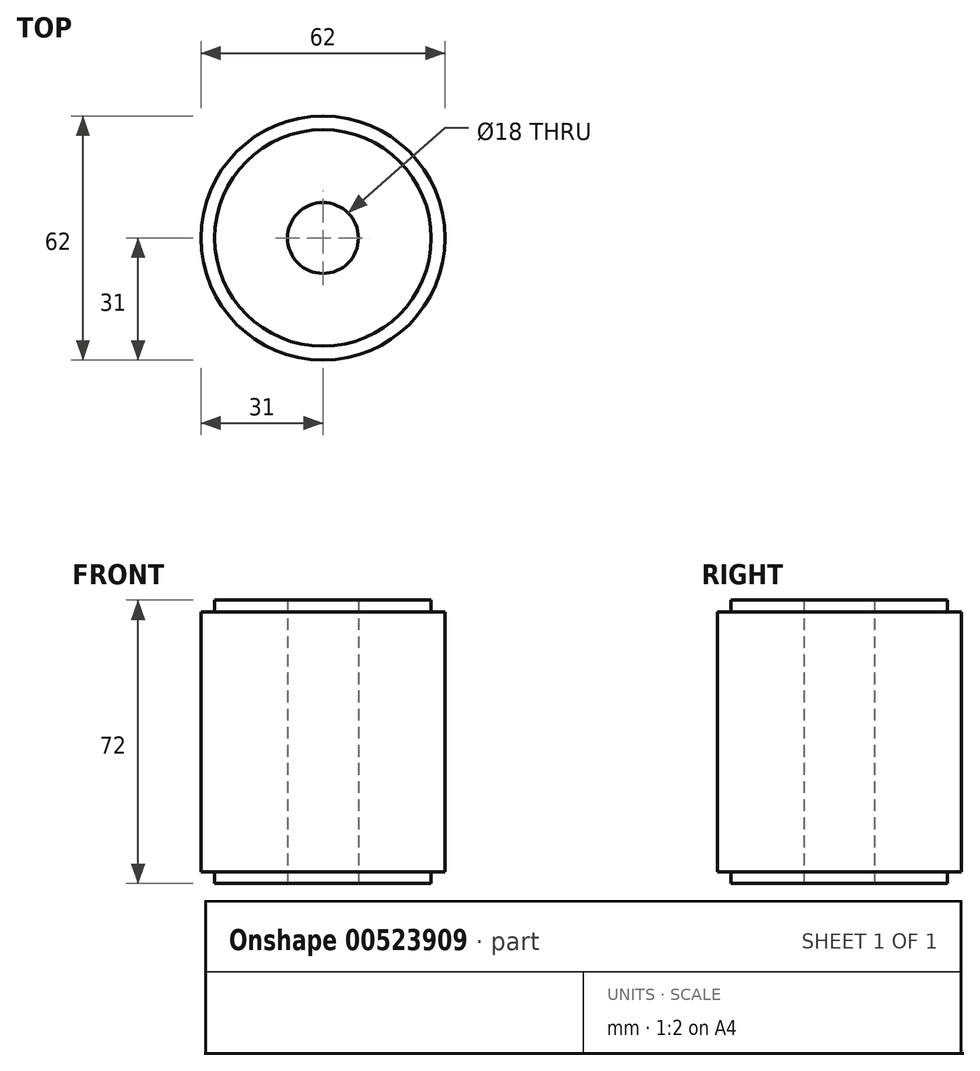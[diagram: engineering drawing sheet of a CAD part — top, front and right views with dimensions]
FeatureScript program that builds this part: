
annotation { "Feature Type Name" : "Feature", "Feature Type Description" : "" }
export const myFeature = defineFeature(function(context is Context, id is Id, definition is map)
    precondition{}
    {
        {
            var Q0;
            Q0=qCreatedBy(makeId("Top.planeOp"),FACE);
            var sketch = newSketch(context, id + "F0", { "sketchPlane" : qUnion([Q0])});
            skCircle(sketch, "E0", {"center": v(0, 0) * mm, "radius": 31 * mm});
            skCircle(sketch, "E1", {"center": v(0, 0) * mm, "radius": 27.5 * mm});
            skCircle(sketch, "E2", {"center": v(0, 0) * mm, "radius": 9 * mm});
            skSolve(sketch);
        }
        {
            var Q0;
            Q0=makeQuery(id+"F0.imprint","IMPRINT",FACE,{"disambiguationData":[TD([[makeQuery(id+"F0.imprint","IMPRINT",EDGE,{"derivedFrom":sQuery(id+"F0.wireOp",EDGE,"E0")}),1.0]])]});
            extrude(context, id + "F1", {"entities" : qUnion([Q0]), "depth" : 69 * mm, "offsetDistance" : 25 * mm, "hasSecondDirection" : true, "secondDirectionOppositeDirection" : false, "secondDirectionDepth" : 3 * mm});
        }
        {
            var Q0;
            Q0=makeQuery(id+"F0.imprint","IMPRINT",FACE,{"disambiguationData":[TD([[makeQuery(id+"F0.imprint","IMPRINT",EDGE,{"derivedFrom":sQuery(id+"F0.wireOp",EDGE,"E1")}),1.0]])]});
            extrude(context, id + "F2", {"entities" : qUnion([Q0]), "operationType" : NewBodyOperationType.ADD, "depth" : 72 * mm, "offsetDistance" : 25 * mm});
        }
    });
